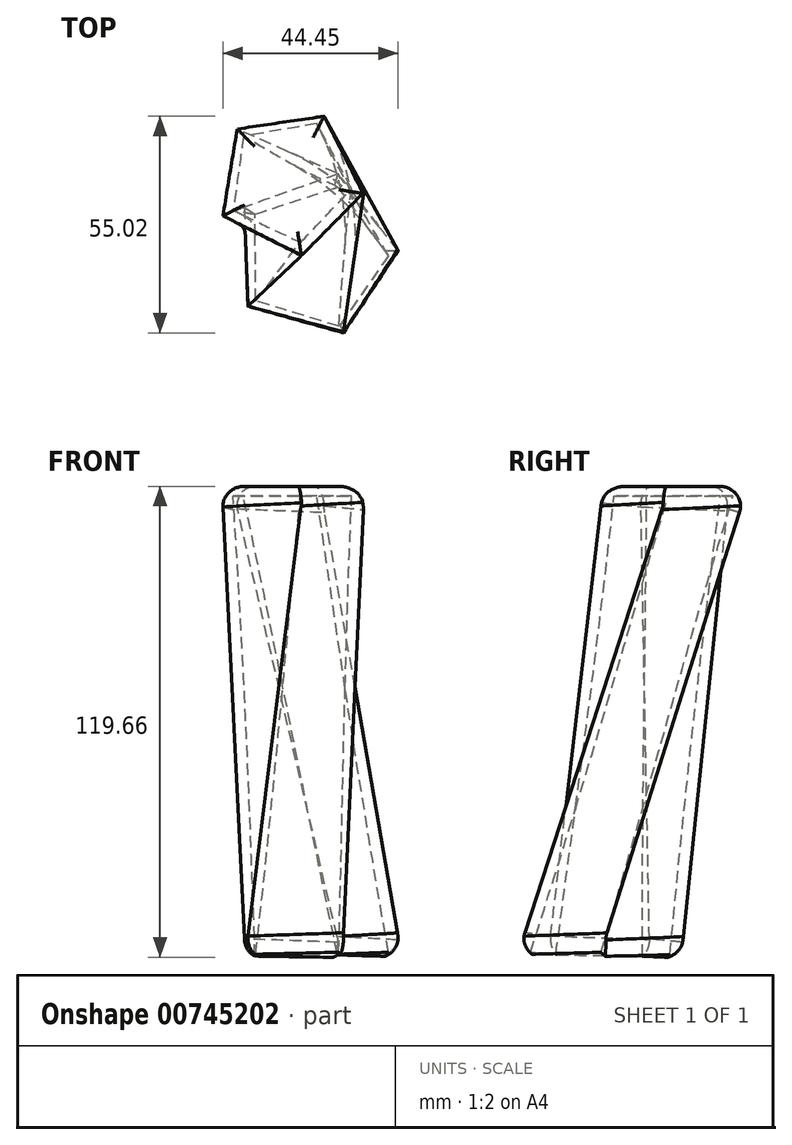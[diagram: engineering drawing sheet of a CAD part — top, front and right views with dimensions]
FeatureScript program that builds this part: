
annotation { "Feature Type Name" : "Feature", "Feature Type Description" : "" }
export const myFeature = defineFeature(function(context is Context, id is Id, definition is map)
    precondition{}
    {
        {
            var Q0;
            Q0=qCreatedBy(makeId("Top.planeOp"),FACE);
            cPlane(context, id + "F0", {"entities" : qUnion([Q0]), "cplaneType" : CPlaneType.OFFSET, "offset" : 120 * mm, "width" : 150 * mm, "height" : 150 * mm});
        }
        {
            var Q0;
            Q0=qCreatedBy(id+"F0.planeOp",FACE);
            var sketch = newSketch(context, id + "F1", { "sketchPlane" : qUnion([Q0])});
            skCircle(sketch, "E0.cCircle", {"center": v(-19.66, 24.84) * mm, "radius": 15.7 * mm, "construction": true});
            skLineSegment(sketch, "E0.0", {"start": v(-0.37, 22.64) * mm, "end": v(-15.8, 5.82) * mm});
            skLineSegment(sketch, "E0.1", {"start": v(-15.8, 5.82) * mm, "end": v(-36.56, 15.29) * mm});
            skLineSegment(sketch, "E0.2", {"start": v(-36.56, 15.29) * mm, "end": v(-33.97, 37.96) * mm});
            skLineSegment(sketch, "E0.3", {"start": v(-33.97, 37.96) * mm, "end": v(-11.6, 42.5) * mm});
            skLineSegment(sketch, "E0.4", {"start": v(-11.6, 42.5) * mm, "end": v(-0.37, 22.64) * mm});
            skPoint(sketch, "E0.0.midPoint", {"position": v(-8.08, 14.23) * mm});
            skSolve(sketch);
        }
        {
            var Q0;
            Q0=qCreatedBy(makeId("Top.planeOp"),FACE);
            var sketch = newSketch(context, id + "F2", { "sketchPlane" : qUnion([Q0])});
            skCircle(sketch, "E1.cCircle", {"center": v(-12.82, 4.7) * mm, "radius": 17.79 * mm, "construction": true});
            skLineSegment(sketch, "E1.0", {"start": v(-30.6, -8.23) * mm, "end": v(-30.6, 17.62) * mm});
            skLineSegment(sketch, "E1.1", {"start": v(-30.6, 17.62) * mm, "end": v(-6.02, 25.6) * mm});
            skLineSegment(sketch, "E1.2", {"start": v(-6.02, 25.6) * mm, "end": v(9.17, 4.7) * mm});
            skLineSegment(sketch, "E1.3", {"start": v(9.17, 4.7) * mm, "end": v(-6.02, -16.21) * mm});
            skLineSegment(sketch, "E1.4", {"start": v(-6.02, -16.21) * mm, "end": v(-30.6, -8.23) * mm});
            skPoint(sketch, "E1.0.midPoint", {"position": v(-30.6, 4.7) * mm});
            skSolve(sketch);
        }
        {
            var Q0;
            Q0=makeQuery(id+"F2.imprint","IMPRINT",FACE,{"disambiguationData":[TD([[makeQuery(id+"F2.imprint","IMPRINT",EDGE,{"derivedFrom":sQuery(id+"F2.wireOp",EDGE,"E1.0")}),-1.0]])]});
            var Q1;
            Q1=makeQuery(id+"F1.imprint","IMPRINT",FACE,{"disambiguationData":[TD([[makeQuery(id+"F1.imprint","IMPRINT",EDGE,{"derivedFrom":sQuery(id+"F1.wireOp",EDGE,"E0.0")}),-1.0]])]});
            var Q2;
            Q2=sQuery(id+"F1.wireOp",VERTEX,"E0.2.start");
            var Q3;
            Q3=sQuery(id+"F2.wireOp",VERTEX,"E1.1.start");
            loft(context, id + "F3", {"sheetProfilesArray" : [{ "sheetProfileEntities" : qUnion([Q0]) }, { "sheetProfileEntities" : qUnion([Q1]) }], "matchConnections" : true, "connections" : [{ "connectionEntities" : qUnion([Q2, Q3]), "connectionEdgeQueries" : qUnion([]), "connectionEdgeParameters" : [] }]});
        }
        {
            var Q0;
            Q0=makeQuery(id+"F3.opLoft","CAP_FACE",FACE,{"disambiguationData":[OSD([makeQuery(id+"F2.imprint","IMPRINT",FACE,{"disambiguationData":[TD([[makeQuery(id+"F2.imprint","IMPRINT",EDGE,{"derivedFrom":sQuery(id+"F2.wireOp",EDGE,"E1.0")}),-1.0]])]})])],"isStart":true});
            shell(context, id + "F4", {"entities" : qUnion([Q0]), "thickness" : 2.5 * mm});
        }
        {
            var Q0;
            Q0=makeQuery(id+"F3.opLoft","MID_CAP_EDGE",EDGE,{"disambiguationData":[OSD([sQuery(id+"F2.wireOp",EDGE,"E1.0"),sQuery(id+"F2.wireOp",EDGE,"E1.1"),sQuery(id+"F2.wireOp",EDGE,"E1.2")])],"capPos":0.0});
            var Q1;
            Q1=makeQuery(id+"F3.opLoft","MID_CAP_EDGE",EDGE,{"disambiguationData":[OSD([sQuery(id+"F2.wireOp",EDGE,"E1.1"),sQuery(id+"F2.wireOp",EDGE,"E1.2"),sQuery(id+"F2.wireOp",EDGE,"E1.3")])],"capPos":0.0});
            var Q2;
            Q2=makeQuery(id+"F3.opLoft","MID_CAP_EDGE",EDGE,{"disambiguationData":[OSD([sQuery(id+"F2.wireOp",EDGE,"E1.2"),sQuery(id+"F2.wireOp",EDGE,"E1.3"),sQuery(id+"F2.wireOp",EDGE,"E1.4")])],"capPos":0.0});
            var Q3;
            Q3=makeQuery(id+"F3.opLoft","MID_CAP_EDGE",EDGE,{"disambiguationData":[OSD([sQuery(id+"F2.wireOp",EDGE,"E1.0"),sQuery(id+"F2.wireOp",EDGE,"E1.3"),sQuery(id+"F2.wireOp",EDGE,"E1.4")])],"capPos":0.0});
            var Q4;
            Q4=makeQuery(id+"F3.opLoft","MID_CAP_EDGE",EDGE,{"disambiguationData":[OSD([sQuery(id+"F2.wireOp",EDGE,"E1.0"),sQuery(id+"F2.wireOp",EDGE,"E1.1"),sQuery(id+"F2.wireOp",EDGE,"E1.4")])],"capPos":0.0});
            var Q5;
            Q5=makeQuery(id+"F3.opLoft","MID_CAP_EDGE",EDGE,{"disambiguationData":[OSD([sQuery(id+"F1.wireOp",EDGE,"E0.1"),sQuery(id+"F1.wireOp",EDGE,"E0.2"),sQuery(id+"F1.wireOp",EDGE,"E0.3")])],"capPos":1.0});
            var Q6;
            Q6=makeQuery(id+"F3.opLoft","MID_CAP_EDGE",EDGE,{"disambiguationData":[OSD([sQuery(id+"F1.wireOp",EDGE,"E0.0"),sQuery(id+"F1.wireOp",EDGE,"E0.1"),sQuery(id+"F1.wireOp",EDGE,"E0.2")])],"capPos":1.0});
            var Q7;
            Q7=makeQuery(id+"F3.opLoft","MID_CAP_EDGE",EDGE,{"disambiguationData":[OSD([sQuery(id+"F1.wireOp",EDGE,"E0.0"),sQuery(id+"F1.wireOp",EDGE,"E0.1"),sQuery(id+"F1.wireOp",EDGE,"E0.4")])],"capPos":1.0});
            var Q8;
            Q8=makeQuery(id+"F3.opLoft","MID_CAP_EDGE",EDGE,{"disambiguationData":[OSD([sQuery(id+"F1.wireOp",EDGE,"E0.0"),sQuery(id+"F1.wireOp",EDGE,"E0.3"),sQuery(id+"F1.wireOp",EDGE,"E0.4")])],"capPos":1.0});
            var Q9;
            Q9=makeQuery(id+"F3.opLoft","MID_CAP_EDGE",EDGE,{"disambiguationData":[OSD([sQuery(id+"F1.wireOp",EDGE,"E0.2"),sQuery(id+"F1.wireOp",EDGE,"E0.3"),sQuery(id+"F1.wireOp",EDGE,"E0.4")])],"capPos":1.0});
            fillet(context, id + "F5", {"entities" : qUnion([Q0, Q1, Q2, Q3, Q4, Q5, Q6, Q7, Q8, Q9]), "radius" : 5 * mm, "tangentPropagation" : true, "allowEdgeOverflow" : false});
        }
    });
